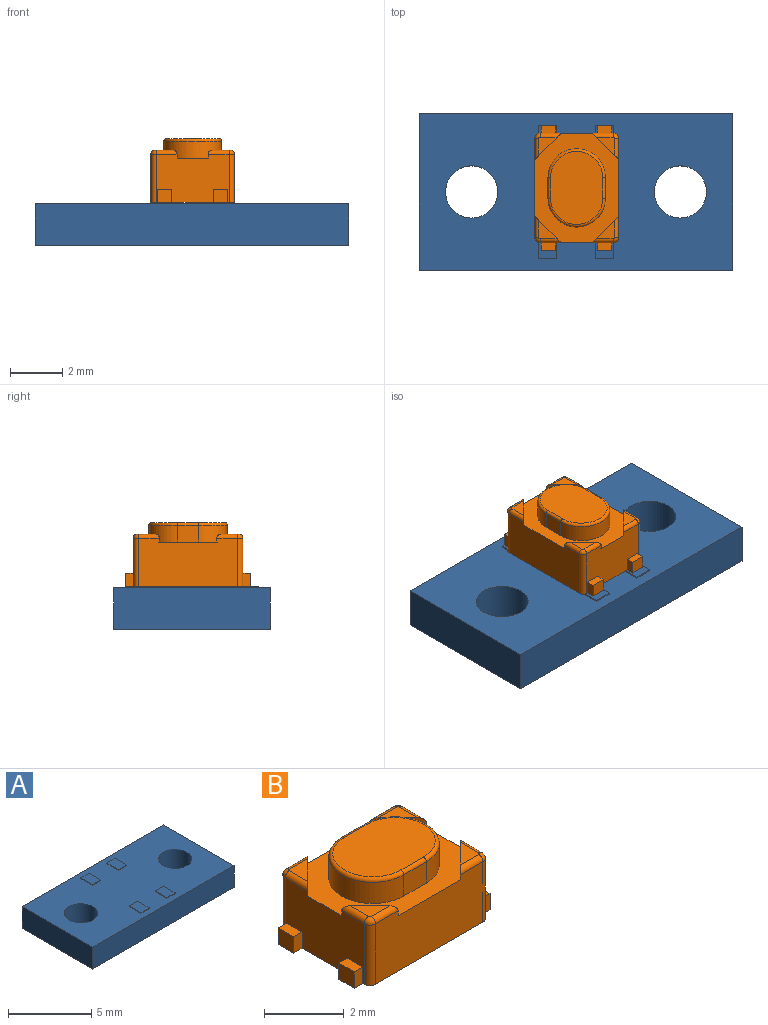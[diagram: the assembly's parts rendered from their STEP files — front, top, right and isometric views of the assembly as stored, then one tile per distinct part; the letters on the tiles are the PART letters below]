
ASSEMBLY  parts=2 mates=1
PART A: 28 faces, bbox 12x6x1.7 mm
  f0: plane 12x6mm, normal (0,0,1), area 62.9mm2, adj f1,f2,f3,f4,f5,f6,f8,f9
  f1: plane 12x1.6mm, normal (0,1,0), area 19.2mm2, adj f0,f2,f6,f7
  f2: plane 6x1.6mm, normal (-1,0,0), area 9.6mm2, adj f0,f1,f3,f7
  f3: plane 12x1.6mm, normal (0,-1,0), area 19.2mm2, adj f0,f2,f6,f7
  f4: cylinder r=1mm len=2mm, axis (0,0,-1), area 10.1mm2, adj f0,f7
  f5: cylinder r=1mm len=2mm, axis (0,0,-1), area 10.1mm2, adj f0,f7
  f6: plane 6x1.6mm, normal (1,0,0), area 9.6mm2, adj f0,f1,f3,f7
  f7: plane 12x6mm, normal (0,0,-1), area 65.7mm2, adj f1,f2,f3,f4,f5,f6
  f8: plane 1x0.05mm, normal (-1,0,0), area 0mm2, adj f0,f9,f11,f12
  f9: plane 0.7x0.05mm, normal (0,-1,0), area 0mm2, adj f0,f8,f10,f12
  f10: plane 1x0.05mm, normal (1,0,0), area 0mm2, adj f0,f9,f11,f12
  f11: plane 0.7x0.05mm, normal (0,1,0), area 0mm2, adj f0,f8,f10,f12
  f12: plane 1x0.7mm, normal (0,0,1), area 0.7mm2, adj f8,f9,f10,f11
  f13: plane 1x0.05mm, normal (-1,0,0), area 0mm2, adj f0,f14,f16,f17
  f14: plane 0.7x0.05mm, normal (0,-1,0), area 0mm2, adj f0,f13,f15,f17
  f15: plane 1x0.05mm, normal (1,0,0), area 0mm2, adj f0,f14,f16,f17
  f16: plane 0.7x0.05mm, normal (0,1,0), area 0mm2, adj f0,f13,f15,f17
  f17: plane 1x0.7mm, normal (0,0,1), area 0.7mm2, adj f13,f14,f15,f16
  f18: plane 1x0.05mm, normal (-1,0,0), area 0mm2, adj f0,f19,f21,f22
  f19: plane 0.7x0.05mm, normal (0,-1,0), area 0mm2, adj f0,f18,f20,f22
  f20: plane 1x0.05mm, normal (1,0,0), area 0mm2, adj f0,f19,f21,f22
  f21: plane 0.7x0.05mm, normal (0,1,0), area 0mm2, adj f0,f18,f20,f22
  f22: plane 1x0.7mm, normal (0,0,1), area 0.7mm2, adj f18,f19,f20,f21
  f23: plane 1x0.05mm, normal (-1,0,0), area 0mm2, adj f0,f24,f26,f27
  f24: plane 0.7x0.05mm, normal (0,-1,0), area 0mm2, adj f0,f23,f25,f27
  f25: plane 1x0.05mm, normal (1,0,0), area 0mm2, adj f0,f24,f26,f27
  f26: plane 0.7x0.05mm, normal (0,1,0), area 0mm2, adj f0,f23,f25,f27
  f27: plane 1x0.7mm, normal (0,0,1), area 0.7mm2, adj f23,f24,f25,f26
PART B: 55 faces, bbox 4.8x3.2x2.5 mm
  f0: plane 4.2x3.2mm, normal (0,0,1), area 5.9mm2, adj f1,f2,f3,f4,f26,f27,f28,f29
  f1: plane 3.8x1.85mm, normal (0,1,0), area 6.7mm2, adj f0,f5,f6,f9,f33,f35,f39,f50
  f2: plane 2.8x1.85mm, normal (-1,0,0), area 4.4mm2, adj f0,f5,f6,f7,f14,f15,f16,f22
  f3: plane 3.8x1.85mm, normal (0,-1,0), area 6.7mm2, adj f0,f5,f7,f8,f31,f37,f42,f47
  f4: plane 2.8x1.85mm, normal (1,0,0), area 4.4mm2, adj f0,f5,f8,f9,f11,f12,f13,f19
  f5: plane 4.8x3.2mm, normal (0,0,-1), area 14.1mm2, adj f1,f2,f3,f4,f6,f7,f8,f9
  f6: cylinder r=0.2mm len=1.85mm, axis (0,0,1), area 0.6mm2, adj f1,f2,f5,f49
  f7: cylinder r=0.2mm len=1.85mm, axis (0,0,-1), area 0.6mm2, adj f2,f3,f5,f46
  f8: cylinder r=0.2mm len=1.85mm, axis (0,0,1), area 0.6mm2, adj f3,f4,f5,f43
  f9: cylinder r=0.2mm len=1.85mm, axis (0,0,-1), area 0.6mm2, adj f1,f4,f5,f40
  f10: plane 0.55x0.5mm, normal (1,0,0), area 0.3mm2, adj f5,f11,f12,f13
  f11: plane 0.55x0.3mm, normal (0,0,1), area 0.2mm2, adj f4,f10,f12,f13
  f12: plane 0.5x0.3mm, normal (0,-1,0), area 0.2mm2, adj f4,f5,f10,f11
  f13: plane 0.5x0.3mm, normal (0,1,0), area 0.2mm2, adj f4,f5,f10,f11
  f14: plane 0.5x0.3mm, normal (0,1,0), area 0.2mm2, adj f2,f5,f16,f17
  f15: plane 0.5x0.3mm, normal (0,-1,0), area 0.2mm2, adj f2,f5,f16,f17
  f16: plane 0.55x0.3mm, normal (0,0,1), area 0.2mm2, adj f2,f14,f15,f17
  f17: plane 0.55x0.5mm, normal (-1,0,0), area 0.3mm2, adj f5,f14,f15,f16
  f18: plane 0.55x0.5mm, normal (1,0,0), area 0.3mm2, adj f5,f19,f20,f21
  f19: plane 0.55x0.3mm, normal (0,0,1), area 0.2mm2, adj f4,f18,f20,f21
  f20: plane 0.5x0.3mm, normal (0,-1,0), area 0.2mm2, adj f4,f5,f18,f19
  f21: plane 0.5x0.3mm, normal (0,1,0), area 0.2mm2, adj f4,f5,f18,f19
  f22: plane 0.55x0.3mm, normal (0,0,1), area 0.2mm2, adj f2,f23,f24,f25
  f23: plane 0.5x0.3mm, normal (0,1,0), area 0.2mm2, adj f2,f5,f22,f25
  f24: plane 0.5x0.3mm, normal (0,-1,0), area 0.2mm2, adj f2,f5,f22,f25
  f25: plane 0.55x0.5mm, normal (-1,0,0), area 0.3mm2, adj f5,f22,f23,f24
  f26: plane 0.8x0.65mm, normal (0,1,0), area 0.5mm2, adj f0,f27,f29,f51
  f27: cylinder r=1.1mm len=2.2mm, axis (0,0,-1), area 2.2mm2, adj f0,f26,f28,f53
  f28: plane 0.8x0.65mm, normal (0,-1,0), area 0.5mm2, adj f0,f27,f29,f54
  f29: cylinder r=1.1mm len=2.2mm, axis (0,0,-1), area 2.2mm2, adj f0,f26,f28,f52
  f30: plane 2.8x2mm, normal (0,0,1), area 4.7mm2, adj f51,f52,f53,f54
  f31: plane 1x1mm, normal (0.71,0.71,0), area 0.4mm2, adj f0,f2,f3,f32,f45,f47
  f32: plane 0.7x0.7mm, normal (0,0,1), area 0.2mm2, adj f31,f45,f46,f47
  f33: plane 1x1mm, normal (0.71,-0.71,0), area 0.4mm2, adj f0,f1,f2,f34,f48,f50
  f34: plane 0.7x0.7mm, normal (0,0,1), area 0.2mm2, adj f33,f48,f49,f50
  f35: plane 1x1mm, normal (-0.71,-0.71,0), area 0.4mm2, adj f0,f1,f4,f36,f39,f41
  f36: plane 0.7x0.7mm, normal (0,0,1), area 0.2mm2, adj f35,f39,f40,f41
  f37: plane 1x1mm, normal (-0.71,0.71,0), area 0.4mm2, adj f0,f3,f4,f38,f42,f44
  f38: plane 0.7x0.7mm, normal (0,0,1), area 0.2mm2, adj f37,f42,f43,f44
  f39: cylinder r=0.15mm len=0.8mm, axis (1,0,0), area 0.2mm2, adj f1,f35,f36,f40
  f40: torus R=0.05mm, axis (0,0,1), area 0.1mm2, adj f9,f36,f39,f41
  f41: cylinder r=0.15mm len=0.8mm, axis (0,-1,0), area 0.2mm2, adj f4,f35,f36,f40
  f42: cylinder r=0.15mm len=0.8mm, axis (-1,0,0), area 0.2mm2, adj f3,f37,f38,f43
  f43: torus R=0.05mm, axis (0,0,1), area 0.1mm2, adj f8,f38,f42,f44
  f44: cylinder r=0.15mm len=0.8mm, axis (0,-1,0), area 0.2mm2, adj f4,f37,f38,f43
  f45: cylinder r=0.15mm len=0.8mm, axis (0,1,0), area 0.2mm2, adj f2,f31,f32,f46
  f46: torus R=0.05mm, axis (0,0,1), area 0.1mm2, adj f7,f32,f45,f47
  f47: cylinder r=0.15mm len=0.8mm, axis (-1,0,0), area 0.2mm2, adj f3,f31,f32,f46
  f48: cylinder r=0.15mm len=0.8mm, axis (0,1,0), area 0.2mm2, adj f2,f33,f34,f49
  f49: torus R=0.05mm, axis (0,0,1), area 0.1mm2, adj f6,f34,f48,f50
  f50: cylinder r=0.15mm len=0.8mm, axis (1,0,0), area 0.2mm2, adj f1,f33,f34,f49
  f51: cylinder r=0.1mm len=0.8mm, axis (1,0,0), area 0.1mm2, adj f26,f30,f52,f53
  f52: torus R=1mm, axis (0,0,1), area 0.5mm2, adj f29,f30,f51,f54
  f53: torus R=1mm, axis (0,0,1), area 0.5mm2, adj f27,f30,f51,f54
  f54: cylinder r=0.1mm len=0.8mm, axis (-1,0,0), area 0.1mm2, adj f28,f30,f52,f53
PLACE A t=(13.25,-13.12,5.36)mm
PLACE B rot(axis=(0,0,-1),90deg) t=(-21.23,-25.73,7.01)mm
MATE fastened B.f5 <-> A.f27  axis (0,0,-1) through (-6.12,-2.59,7.01)mm
